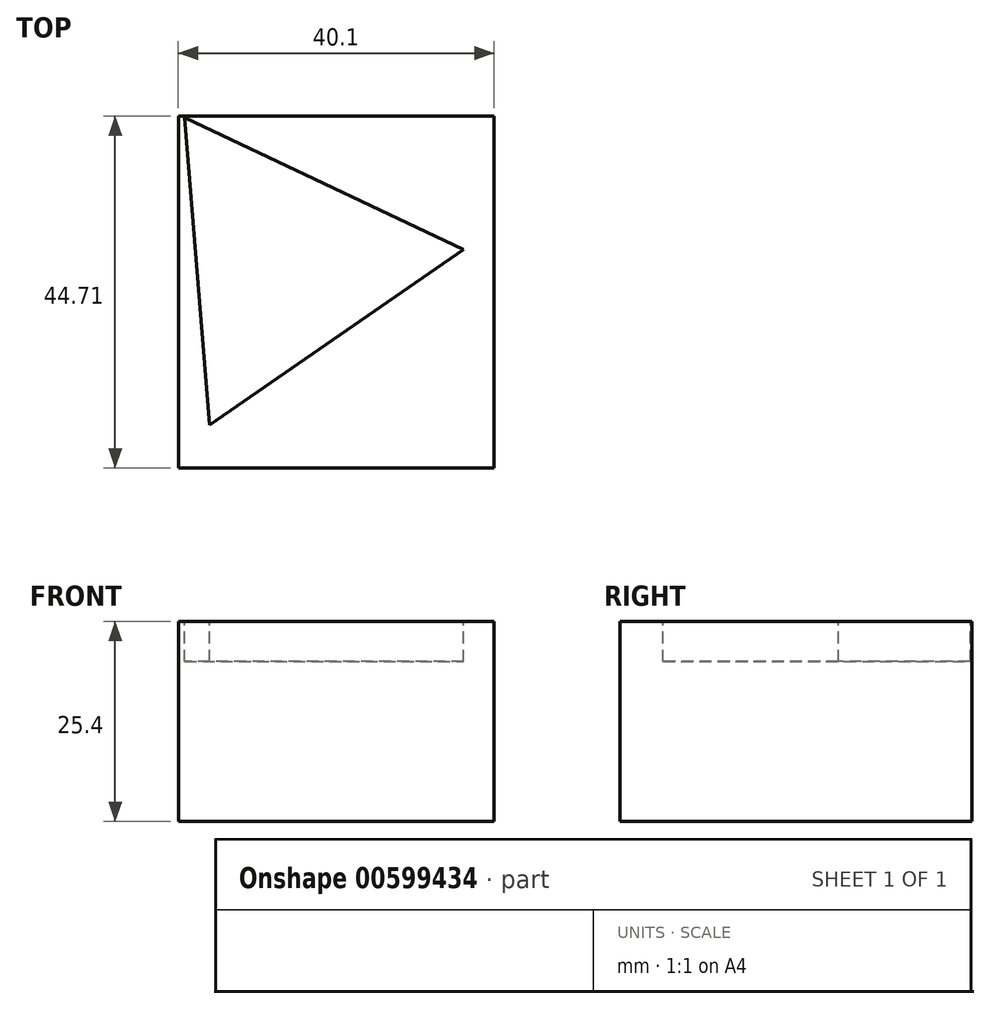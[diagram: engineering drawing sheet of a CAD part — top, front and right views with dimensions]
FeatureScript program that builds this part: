
annotation { "Feature Type Name" : "Feature", "Feature Type Description" : "" }
export const myFeature = defineFeature(function(context is Context, id is Id, definition is map)
    precondition{}
    {
        {
            var Q0;
            Q0=qCreatedBy(makeId("Top.planeOp"),FACE);
            var sketch = newSketch(context, id + "F0", { "sketchPlane" : qUnion([Q0])});
            skLineSegment(sketch, "E0.bottom", {"start": v(0, 0) * mm, "end": v(-40.1, 0) * mm});
            skLineSegment(sketch, "E0.top", {"start": v(0, 44.7) * mm, "end": v(-40.1, 44.7) * mm});
            skLineSegment(sketch, "E0.left", {"start": v(0, 0) * mm, "end": v(0, 44.7) * mm});
            skLineSegment(sketch, "E0.right", {"start": v(-40.1, 0) * mm, "end": v(-40.1, 44.7) * mm});
            skSolve(sketch);
        }
        {
            var Q0;
            Q0 = qSketchRegion(id + "F0", true);
            extrude(context, id + "F1", {"entities" : qUnion([Q0]), "depth" : 25.4 * mm, "offsetDistance" : 25.4 * mm});
        }
        {
            var Q0;
            Q0=makeQuery(id+"F1.opExtrude","CAP_FACE",FACE,{"disambiguationData":[OSD([sQuery(id+"F0.wireOp",EDGE,"E0.bottom"),sQuery(id+"F0.wireOp",EDGE,"E0.top"),sQuery(id+"F0.wireOp",EDGE,"E0.left"),sQuery(id+"F0.wireOp",EDGE,"E0.right")])],"isStart":false});
            var sketch = newSketch(context, id + "F2", { "sketchPlane" : qUnion([Q0])});
            skCircle(sketch, "E1.cCircle", {"center": v(-26.43, 25.91) * mm, "radius": 11.3 * mm, "construction": true});
            skLineSegment(sketch, "E1.0", {"start": v(-3.9, 27.75) * mm, "end": v(-36.1, 5.48) * mm});
            skLineSegment(sketch, "E1.1", {"start": v(-36.1, 5.48) * mm, "end": v(-39.28, 44.5) * mm});
            skLineSegment(sketch, "E1.2", {"start": v(-39.28, 44.5) * mm, "end": v(-3.9, 27.75) * mm});
            skPoint(sketch, "E1.0.midPoint", {"position": v(-20, 16.61) * mm});
            skSolve(sketch);
        }
        {
            var Q0;
            Q0=makeQuery(id+"F2.imprint","IMPRINT",FACE,{"disambiguationData":[TD([[makeQuery(id+"F2.imprint","IMPRINT",EDGE,{"derivedFrom":sQuery(id+"F2.wireOp",EDGE,"E1.0")}),-1.0]])]});
            extrude(context, id + "F3", {"entities" : qUnion([Q0]), "operationType" : NewBodyOperationType.REMOVE, "oppositeDirection" : true, "depth" : 5.08 * mm, "offsetDistance" : 25.4 * mm});
        }
    });
